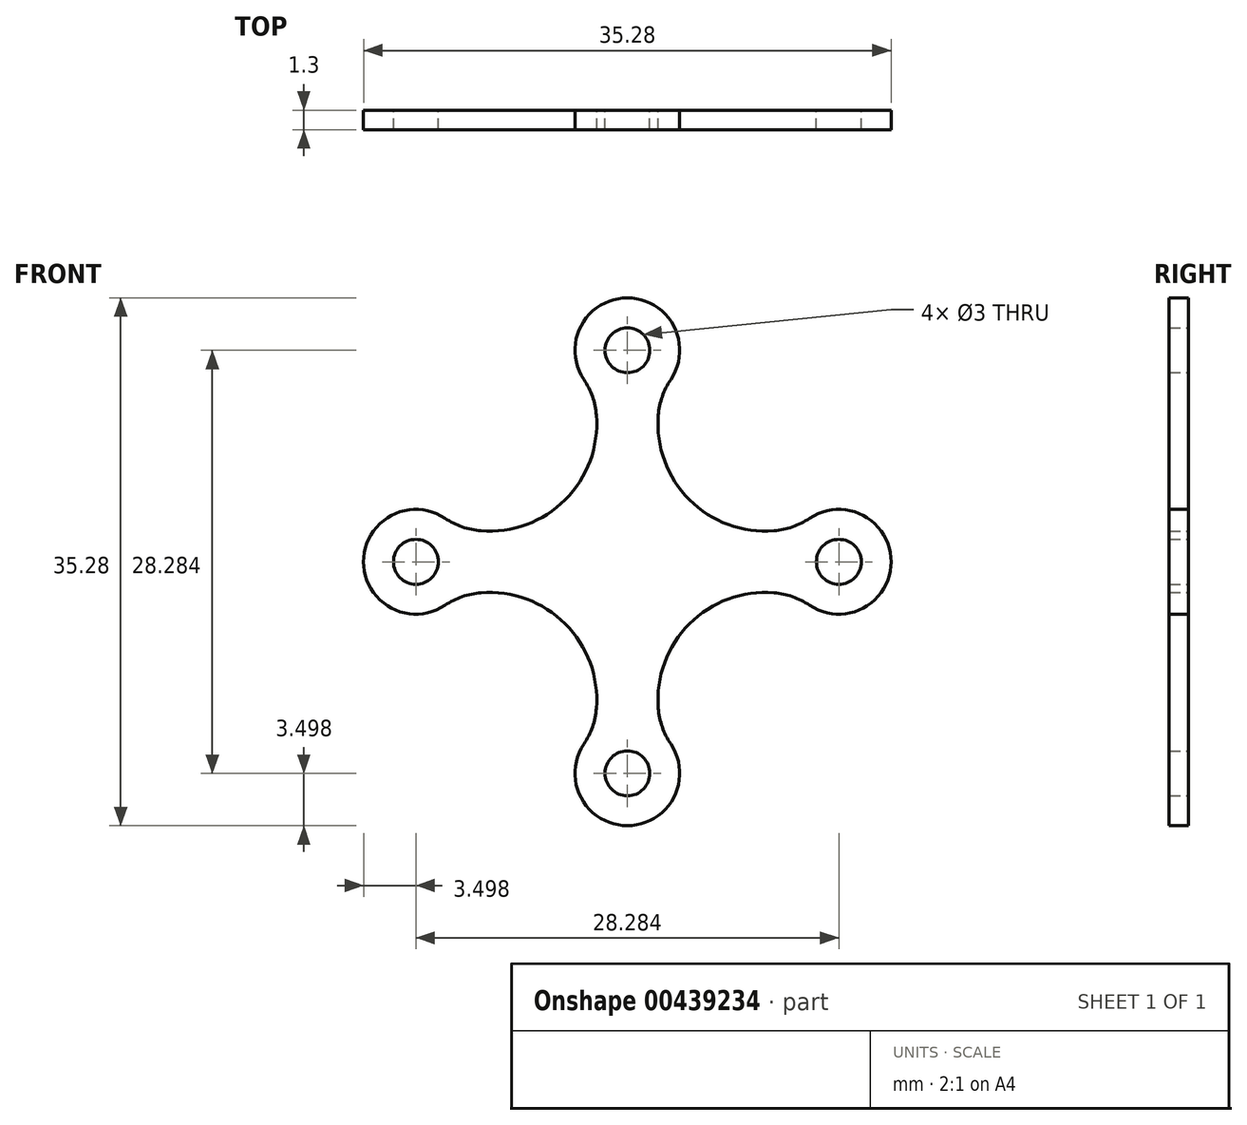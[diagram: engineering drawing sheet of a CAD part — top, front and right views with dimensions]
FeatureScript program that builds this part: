
annotation { "Feature Type Name" : "Feature", "Feature Type Description" : "" }
export const myFeature = defineFeature(function(context is Context, id is Id, definition is map)
    precondition{}
    {
        {
            var Q0;
            Q0=qCreatedBy(makeId("Front.planeOp"),FACE);
            var sketch = newSketch(context, id + "F0", { "sketchPlane" : qUnion([Q0])});
            skPoint(sketch, "E0.middle", {"position": v(0, 0) * mm});
            skCircle(sketch, "E1", {"center": v(0, 14.14) * mm, "radius": 1.5 * mm});
            skCircle(sketch, "E2", {"center": v(14.14, 0) * mm, "radius": 1.5 * mm});
            skCircle(sketch, "E3", {"center": v(0, -14.14) * mm, "radius": 1.5 * mm});
            skCircle(sketch, "E4", {"center": v(-14.14, 0) * mm, "radius": 1.5 * mm});
            skArc(sketch, "E5.0", {"start": v(-12.19, 2.9) * mm, "mid": v(-17.64, 0) * mm, "end": v(-12.19, -2.9) * mm});
            skArc(sketch, "E6.0", {"start": v(2.9, 12.19) * mm, "mid": v(0, 17.64) * mm, "end": v(-2.9, 12.19) * mm});
            skArc(sketch, "E7.0", {"start": v(-2.9, -12.19) * mm, "mid": v(0, -17.64) * mm, "end": v(2.9, -12.19) * mm});
            skArc(sketch, "E8.0", {"start": v(12.19, -2.9) * mm, "mid": v(17.64, 0) * mm, "end": v(12.19, 2.9) * mm});
            skArc(sketch, "E9", {"start": v(-2.07, -9.8) * mm, "mid": v(-4.15, -4.15) * mm, "end": v(-9.8, -2.07) * mm});
            skArc(sketch, "E10.MirrorCS", {"start": v(-2.07, 9.8) * mm, "mid": v(-4.15, 4.15) * mm, "end": v(-9.8, 2.07) * mm});
            skArc(sketch, "E11.MirrorCS", {"start": v(2.07, 9.8) * mm, "mid": v(4.15, 4.15) * mm, "end": v(9.8, 2.07) * mm});
            skArc(sketch, "E12.MirrorCS", {"start": v(2.07, -9.8) * mm, "mid": v(4.15, -4.15) * mm, "end": v(9.8, -2.07) * mm});
            skPoint(sketch, "E13.visualSharp", {"position": v(-2.47, -11.67) * mm});
            skArc(sketch, "E13.filletArc", {"start": v(-2.9, -12.19) * mm, "mid": v(-2.33, -11.05) * mm, "end": v(-2.07, -9.8) * mm});
            skPoint(sketch, "E14.visualSharp", {"position": v(2.47, -11.67) * mm});
            skArc(sketch, "E14.filletArc", {"start": v(2.07, -9.8) * mm, "mid": v(2.33, -11.05) * mm, "end": v(2.9, -12.19) * mm});
            skPoint(sketch, "E15.visualSharp", {"position": v(-11.67, -2.47) * mm});
            skArc(sketch, "E15.filletArc", {"start": v(-9.8, -2.07) * mm, "mid": v(-11.05, -2.33) * mm, "end": v(-12.19, -2.9) * mm});
            skPoint(sketch, "E16.visualSharp", {"position": v(-11.67, 2.47) * mm});
            skArc(sketch, "E16.filletArc", {"start": v(-12.19, 2.9) * mm, "mid": v(-11.05, 2.33) * mm, "end": v(-9.8, 2.07) * mm});
            skPoint(sketch, "E17.visualSharp", {"position": v(-2.47, 11.67) * mm});
            skArc(sketch, "E17.filletArc", {"start": v(-2.07, 9.8) * mm, "mid": v(-2.33, 11.05) * mm, "end": v(-2.9, 12.19) * mm});
            skPoint(sketch, "E18.visualSharp", {"position": v(2.47, 11.67) * mm});
            skArc(sketch, "E18.filletArc", {"start": v(2.9, 12.19) * mm, "mid": v(2.33, 11.05) * mm, "end": v(2.07, 9.8) * mm});
            skPoint(sketch, "E19.visualSharp", {"position": v(11.67, -2.47) * mm});
            skArc(sketch, "E19.filletArc", {"start": v(12.19, -2.9) * mm, "mid": v(11.05, -2.33) * mm, "end": v(9.8, -2.07) * mm});
            skPoint(sketch, "E20.visualSharp", {"position": v(11.67, 2.47) * mm});
            skArc(sketch, "E20.filletArc", {"start": v(9.8, 2.07) * mm, "mid": v(11.05, 2.33) * mm, "end": v(12.19, 2.9) * mm});
            skSolve(sketch);
        }
        {
            var Q0;
            Q0=makeQuery(id+"F0.imprint","IMPRINT",FACE,{"disambiguationData":[TD([[makeQuery(id+"F0.imprint","IMPRINT",EDGE,{"derivedFrom":sQuery(id+"F0.wireOp",EDGE,"E1")}),-1.0]])]});
            extrude(context, id + "F1", {"entities" : qUnion([Q0]), "depth" : 1.3 * mm, "offsetDistance" : 25 * mm});
        }
    });
